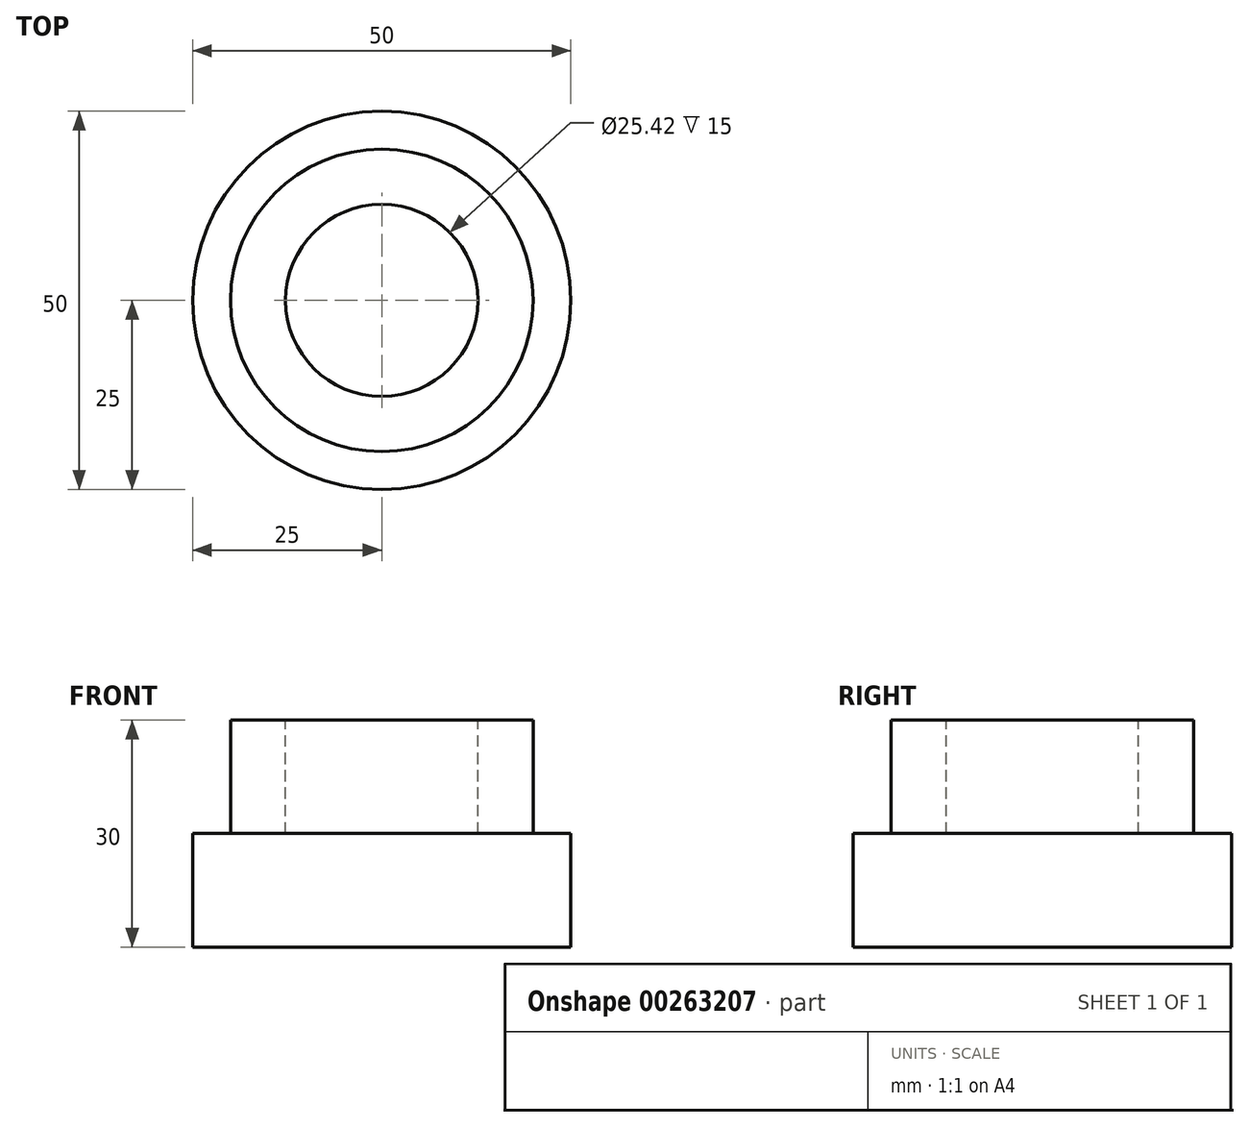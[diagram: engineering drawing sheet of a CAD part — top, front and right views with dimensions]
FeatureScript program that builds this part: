
annotation { "Feature Type Name" : "Feature", "Feature Type Description" : "" }
export const myFeature = defineFeature(function(context is Context, id is Id, definition is map)
    precondition{}
    {
        {
            assignVariable(context, id + "F0", {"name" : "Zone", "anyValue" : 15});
        }
        {
            assignVariable(context, id + "F1", {"name" : "Zdos", "anyValue" : 30});
        }
        {
            var Q0;
            Q0=qCreatedBy(makeId("Top.planeOp"),FACE);
            var sketch = newSketch(context, id + "F2", { "sketchPlane" : qUnion([Q0])});
            skCircle(sketch, "E0", {"center": v(0, 0) * mm, "radius": 25 * mm});
            skCircle(sketch, "E1", {"center": v(0, 0) * mm, "radius": 20 * mm});
            skSolve(sketch);
        }
        {
            var Q0;
            Q0=makeQuery(id+"F2.imprint","IMPRINT",FACE,{"disambiguationData":[TD([[makeQuery(id+"F2.imprint","IMPRINT",EDGE,{"derivedFrom":sQuery(id+"F2.wireOp",EDGE,"E0")}),1.0]])]});
            extrude(context, id + "F3", {"entities" : qUnion([Q0]), "depth" : (getVariable(context, 'Zone')) * mm});
        }
        {
            var Q0;
            Q0=makeQuery(id+"F2.imprint","IMPRINT",FACE,{"disambiguationData":[TD([[makeQuery(id+"F2.imprint","IMPRINT",EDGE,{"derivedFrom":sQuery(id+"F2.wireOp",EDGE,"E1")}),1.0]])]});
            extrude(context, id + "F4", {"entities" : qUnion([Q0]), "operationType" : NewBodyOperationType.ADD, "depth" : (getVariable(context, 'Zdos')) * mm});
        }
        {
            var Q0;
            Q0=makeQuery(id+"F4.opExtrude","CAP_FACE",FACE,{"disambiguationData":[OSD([sQuery(id+"F2.wireOp",EDGE,"E1")])],"isStart":false});
            var sketch = newSketch(context, id + "F5", { "sketchPlane" : qUnion([Q0])});
            skCircle(sketch, "E2", {"center": v(0, 0) * mm, "radius": 12.7 * mm});
            skSolve(sketch);
        }
        {
            var Q0;
            Q0=makeQuery(id+"F5.imprint","IMPRINT",FACE,{"disambiguationData":[TD([[makeQuery(id+"F5.imprint","IMPRINT",EDGE,{"derivedFrom":sQuery(id+"F5.wireOp",EDGE,"E2")}),1.0]])]});
            extrude(context, id + "F6", {"entities" : qUnion([Q0]), "operationType" : NewBodyOperationType.REMOVE, "oppositeDirection" : true, "depth" : (getVariable(context, 'Zone')) * mm});
        }
    });
